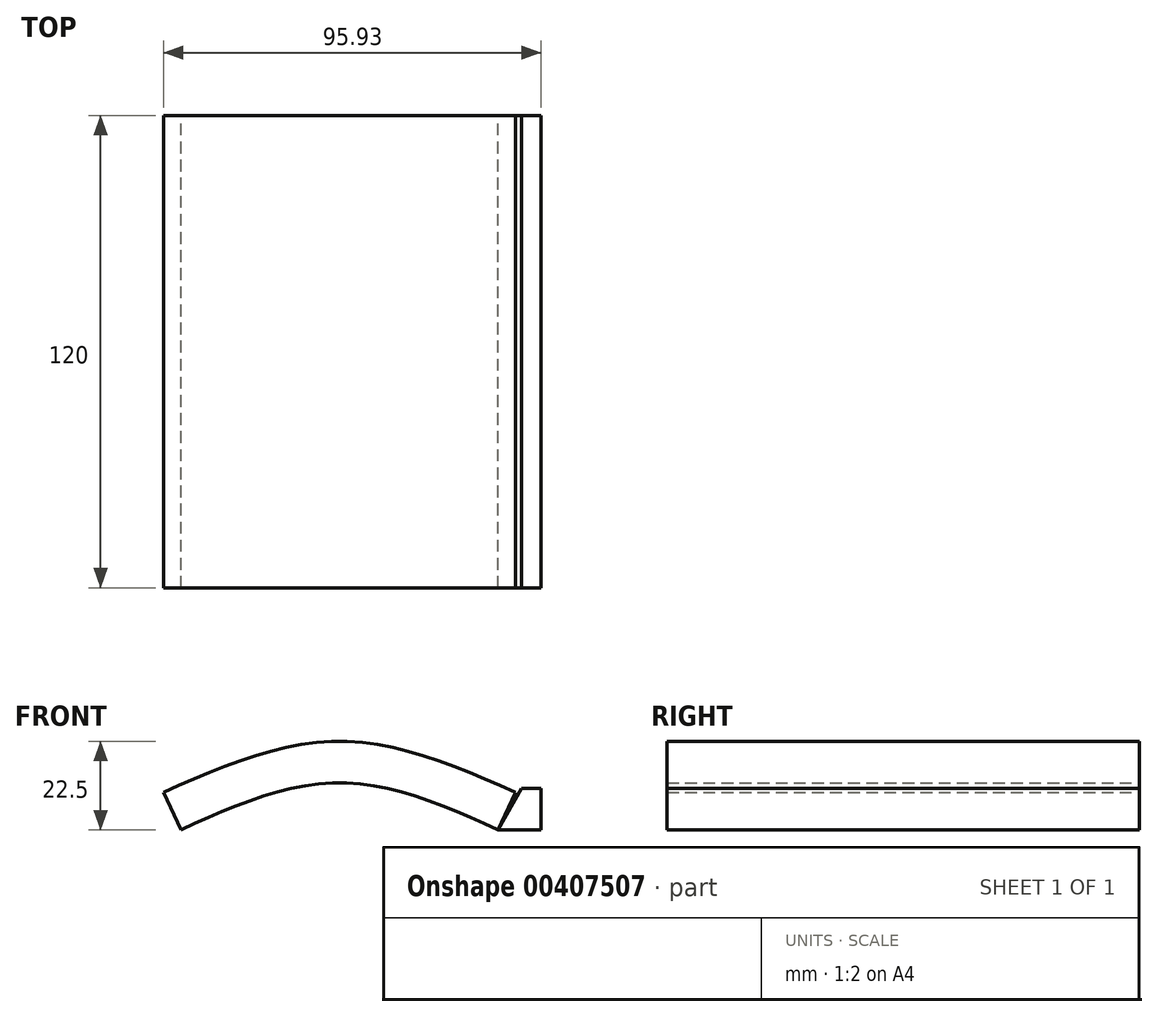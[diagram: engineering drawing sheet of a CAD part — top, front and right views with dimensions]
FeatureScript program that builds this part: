
annotation { "Feature Type Name" : "Feature", "Feature Type Description" : "" }
export const myFeature = defineFeature(function(context is Context, id is Id, definition is map)
    precondition{}
    {
        {
            var Q0;
            Q0=qCreatedBy(makeId("Front.planeOp"),FACE);
            var sketch = newSketch(context, id + "F0", { "sketchPlane" : qUnion([Q0])});
            skLineSegment(sketch, "E0.bottom", {"start": v(-40.25, 11.5) * mm, "end": v(40.25, 11.5) * mm, "construction": true});
            skLineSegment(sketch, "E0.top", {"start": v(-40.25, -11.5) * mm, "end": v(40.25, -11.5) * mm, "construction": true});
            skLineSegment(sketch, "E0.left", {"start": v(-40.25, 11.5) * mm, "end": v(-40.25, -11.5) * mm, "construction": true});
            skLineSegment(sketch, "E0.right", {"start": v(40.25, 11.5) * mm, "end": v(40.25, -11.5) * mm, "construction": true});
            skPoint(sketch, "E0.middle", {"position": v(0, 0) * mm});
            skLineSegment(sketch, "E1", {"start": v(0, -11.5) * mm, "end": v(0, 23.5) * mm, "construction": true});
            skPoint(sketch, "E1.endSnap0", {"position": v(0, 11.5) * mm});
            skFitSpline(sketch, "E2", {"points": [v(-40.25, 11.5) * mm, v(0, 23.5) * mm, v(40.25, 11.5) * mm], "startDerivative": vector(80.5, 37.5) * mm, "endDerivative": vector(80.5, -37.5) * mm});
            skLineSegment(sketch, "E3", {"start": v(26.83, 17.75) * mm, "end": v(40.25, 11.5) * mm});
            skLineSegment(sketch, "E4", {"start": v(40.25, 11.5) * mm, "end": v(44.68, 21.02) * mm});
            skLineSegment(sketch, "E5", {"start": v(-40.25, 11.5) * mm, "end": v(-52.69, 5.7) * mm, "construction": true});
            skLineSegment(sketch, "E6", {"start": v(-40.25, 11.5) * mm, "end": v(-44.68, 21.02) * mm});
            skLineSegment(sketch, "E7", {"start": v(0, 23.5) * mm, "end": v(0, 34) * mm, "construction": true});
            skFitSpline(sketch, "E8", {"points": [v(-44.68, 21.02) * mm, v(0, 34) * mm, v(44.68, 21.02) * mm], "startDerivative": vector(89.37, 40.45) * mm, "endDerivative": vector(89.37, -40.45) * mm});
            skLineSegment(sketch, "E9", {"start": v(40.25, 11.5) * mm, "end": v(51.25, 11.5) * mm});
            skLineSegment(sketch, "E10", {"start": v(51.25, 11.5) * mm, "end": v(51.25, 22) * mm});
            skLineSegment(sketch, "E11", {"start": v(51.25, 22) * mm, "end": v(46.29, 22) * mm});
            skLineSegment(sketch, "E12", {"start": v(46.29, 22) * mm, "end": v(40.25, 11.5) * mm});
            skSolve(sketch);
        }
        {
            var Q0;
            Q0 = qSketchRegion(id + "F0", true);
            extrude(context, id + "F1", {"entities" : qUnion([Q0]), "depth" : 120 * mm});
        }
    });
